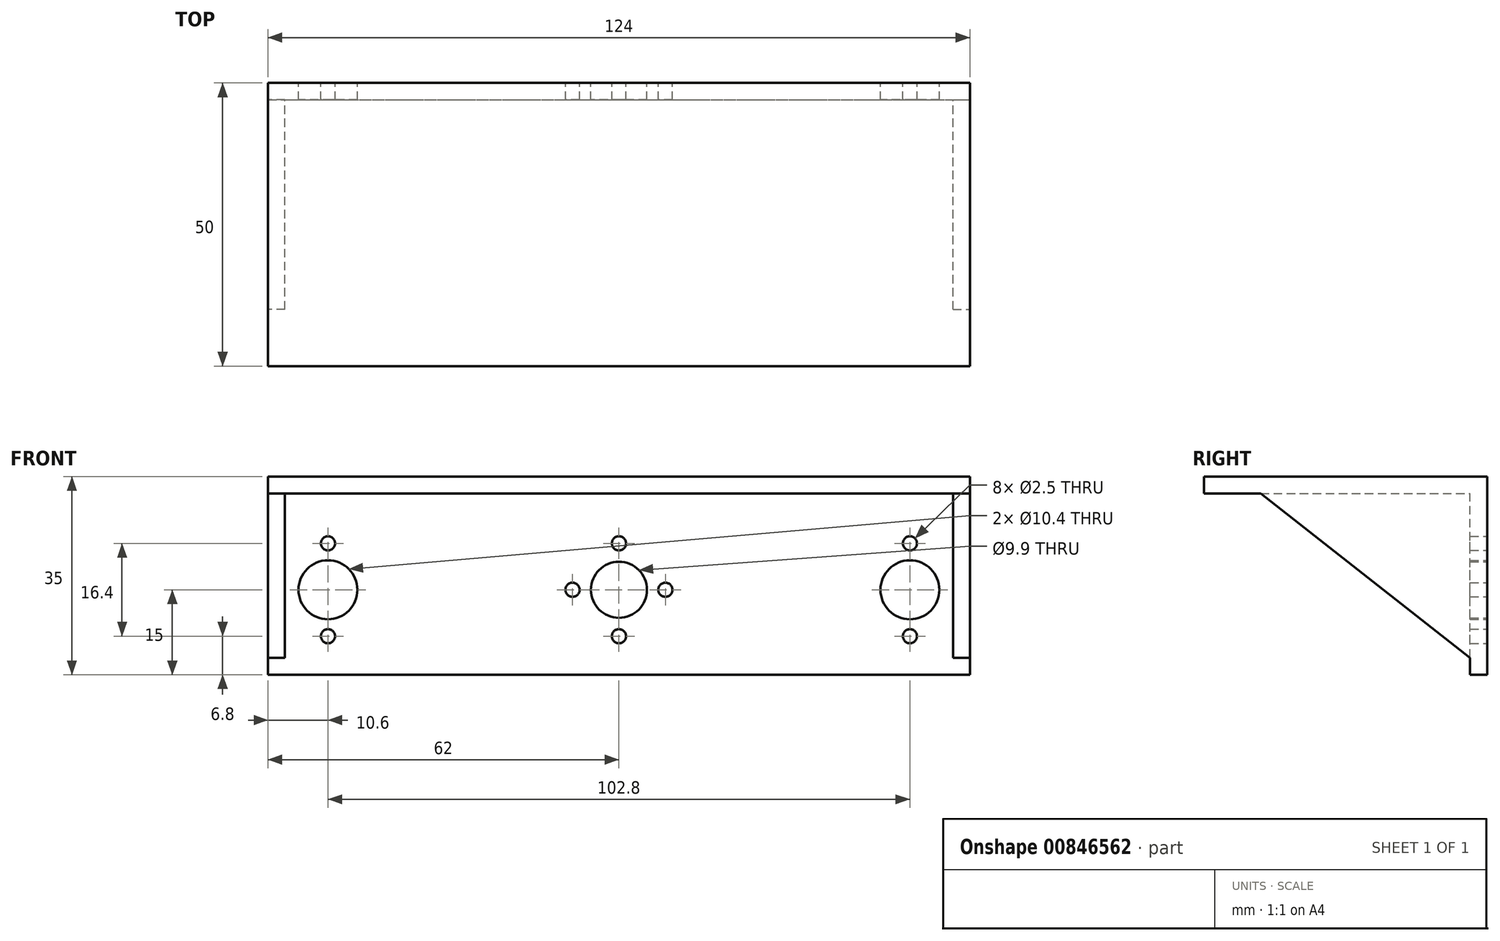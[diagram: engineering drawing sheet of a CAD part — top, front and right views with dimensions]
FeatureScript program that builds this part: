
annotation { "Feature Type Name" : "Feature", "Feature Type Description" : "" }
export const myFeature = defineFeature(function(context is Context, id is Id, definition is map)
    precondition{}
    {
        {
            var Q0;
            Q0=qCreatedBy(makeId("Front.planeOp"),FACE);
            var sketch = newSketch(context, id + "F0", { "sketchPlane" : qUnion([Q0])});
            skPoint(sketch, "E0.middle", {"position": v(0, 0) * mm});
            skCircle(sketch, "E1", {"center": v(0, 0) * mm, "radius": 4.95 * mm});
            skCircle(sketch, "E2", {"center": v(8.2, 0) * mm, "radius": 1.25 * mm});
            skCircle(sketch, "E3", {"center": v(0, 8.2) * mm, "radius": 1.25 * mm});
            skCircle(sketch, "E4", {"center": v(-8.2, 0) * mm, "radius": 1.25 * mm});
            skCircle(sketch, "E5", {"center": v(0, -8.2) * mm, "radius": 1.25 * mm});
            skLineSegment(sketch, "E6.bottom", {"start": v(-62, -15) * mm, "end": v(62, -15) * mm});
            skLineSegment(sketch, "E6.top", {"start": v(-62, 20) * mm, "end": v(62, 20) * mm});
            skLineSegment(sketch, "E6.left", {"start": v(-62, -15) * mm, "end": v(-62, 20) * mm});
            skLineSegment(sketch, "E6.right", {"start": v(62, -15) * mm, "end": v(62, 20) * mm});
            skLineSegment(sketch, "E7", {"start": v(-62, 17) * mm, "end": v(62, 17) * mm});
            skCircle(sketch, "E8", {"center": v(-51.4, 0) * mm, "radius": 5.2 * mm});
            skCircle(sketch, "E9", {"center": v(51.4, 0) * mm, "radius": 5.2 * mm});
            skCircle(sketch, "E10", {"center": v(-51.4, 8.2) * mm, "radius": 1.25 * mm});
            skCircle(sketch, "E11", {"center": v(-51.4, -8.2) * mm, "radius": 1.25 * mm});
            skCircle(sketch, "E12", {"center": v(51.4, 8.2) * mm, "radius": 1.25 * mm});
            skCircle(sketch, "E13", {"center": v(51.4, -8.2) * mm, "radius": 1.25 * mm});
            skSolve(sketch);
        }
        {
            var Q0;
            Q0=makeQuery(id+"F0.imprint","IMPRINT",FACE,{"disambiguationData":[TD([[makeQuery(id+"F0.imprint","IMPRINT",EDGE,{"derivedFrom":sQuery(id+"F0.wireOp",EDGE,"E1")}),-1.0]])]});
            extrude(context, id + "F1", {"entities" : qUnion([Q0]), "depth" : 3 * mm, "offsetDistance" : 25 * mm});
        }
        {
            var Q0;
            {var subQ0=sQuery(id+"F0.wireOp",EDGE,"E6.top");Q0=makeQuery(id+"F0.imprint","IMPRINT",FACE,{"disambiguationData":[TD([[makeQuery(id+"F0.imprint","IMPRINT",EDGE,{"derivedFrom":subQ0}),-1.0]])]});}
            extrude(context, id + "F2", {"entities" : qUnion([Q0]), "operationType" : NewBodyOperationType.ADD, "depth" : 50 * mm, "offsetDistance" : 25 * mm});
        }
        {
            var Q0;
            {var subQ0=sQuery(id+"F0.wireOp",EDGE,"E6.right");Q0=makeQuery(id+"F2.boolean.opBoolean","MERGE",FACE,{"derivedFrom":[makeQuery(id+"F1.opExtrude","SWEPT_FACE",FACE,{"disambiguationData":[OSD([subQ0])]}),makeQuery(id+"F2.opExtrude","SWEPT_FACE",FACE,{"disambiguationData":[OSD([subQ0])]})]});}
            var sketch = newSketch(context, id + "F3", { "sketchPlane" : qUnion([Q0])});
            skLineSegment(sketch, "E14", {"start": v(-40, 17) * mm, "end": v(-3, -12) * mm});
            skSolve(sketch);
        }
        {
            var Q0;
            {var subQ0=sQuery(id+"F0.wireOp",EDGE,"E6.left");Q0=makeQuery(id+"F2.boolean.opBoolean","MERGE",FACE,{"derivedFrom":[makeQuery(id+"F1.opExtrude","SWEPT_FACE",FACE,{"disambiguationData":[OSD([subQ0])]}),makeQuery(id+"F2.opExtrude","SWEPT_FACE",FACE,{"disambiguationData":[OSD([subQ0])]})]});}
            var sketch = newSketch(context, id + "F4", { "sketchPlane" : qUnion([Q0])});
            skLineSegment(sketch, "E15", {"start": v(3, -12) * mm, "end": v(40, 17) * mm});
            skSolve(sketch);
        }
        {
            var Q0;
            {var subQ0=sQuery(id+"F4.wireOp",EDGE,"E15");Q0=makeQuery(id+"F4.imprint","IMPRINT",FACE,{"disambiguationData":[TD([[makeQuery(id+"F4.imprint","IMPRINT",EDGE,{"derivedFrom":subQ0}),1.0]])]});}
            extrude(context, id + "F5", {"entities" : qUnion([Q0]), "operationType" : NewBodyOperationType.ADD, "oppositeDirection" : true, "depth" : 3 * mm, "offsetDistance" : 25 * mm});
        }
        {
            var Q0;
            {var subQ0=sQuery(id+"F3.wireOp",EDGE,"E14");Q0=makeQuery(id+"F3.imprint","IMPRINT",FACE,{"disambiguationData":[TD([[makeQuery(id+"F3.imprint","IMPRINT",EDGE,{"derivedFrom":subQ0}),1.0]])]});}
            extrude(context, id + "F6", {"entities" : qUnion([Q0]), "operationType" : NewBodyOperationType.ADD, "oppositeDirection" : true, "depth" : 3 * mm, "offsetDistance" : 25 * mm});
        }
    });
